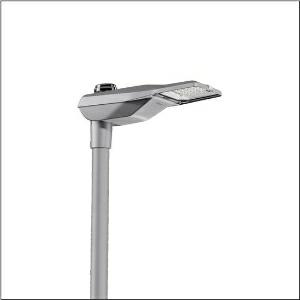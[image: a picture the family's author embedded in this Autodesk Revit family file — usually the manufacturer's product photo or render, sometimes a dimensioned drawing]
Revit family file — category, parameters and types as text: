
# Revit family: streetlight_sl_21_micro___p0_8a_5xe5u27n08db_ddcc
name_source: partatom
category: Lighting Fixtures
units: mm (PartAtom-declared; Revit-internal decimal feet)

## family parameters
Cut with Voids When Loaded = No
Host = Face
Light Source = No
Part Type = Normal
Room Calculation Point = No
Round Connector Dimension = Use Diameter
Shared = No

## types (1)
- --- (1 x LED, 4180 lm, 39.1 W, 2200K)
    Apparent Load = 39 VA
    CIE Flux Codes = 33 69 96 100 100
    Color Rendering = 70
    Color Temperature = 2200K
    Default Elevation = 1800 mm
    Description = Streetlight SL 21 micro, mast luminaire, primary light control with lens, of PMMA, primary optical cover: cover, of toughened safety glass, transparent, light distribution: P0.8a, light emission: direct distribution, primary light characteristic: asymmetric, installation type: post-top, LED, 3G 1.5mm², High Power LED, rated luminous flux: 4.180lm, luminous efficacy: 107lm/W, light colour: 722, colour temperature: 2200K, control gear: NEMA (7pin), control: flexible luminous flux parameterisation, time-dependent luminous flux control, constant luminous flux control, pre-setting: linear dimming characteristic, overheat protection, mains connection: 230..240V, AC, 50/60Hz, connection cable pre-assembled, cable length: 6,5m, wiring characteristics: H07RN-F, start of lifetime: 39W, end of service life: 41W, reduction: 18W, luminaire housing, of diecast aluminium (EN AC-44300), powder-coated, SITECO metallic grey (DB 702S), corrosivity category C5 high according to DIN EN ISO 12944, multi-level sealing system, sealing non-destructively replaceable, inclination adjustable: 0°, 5°, 10°, 15°, length: 528mm, width: 235mm, height: 110mm, spigot size: 76/60mm (post-top), mounting height: 4..8m, protection rating (complete): IP66, insulation class (complete): insulation class I (protective earthing), certification: CE, ENEC, ENEC+, VDE, impact resistance: IK10, permissible operating ambient temperature for outdoor applications: -40..+50°C, standard-compliant lighting for roads and squares, packaging unit: 1 piece

Light Distribution: P0.8a
    Height = 110 mm
    Lamp = 1 x LED
    Lamp Light Flux = 4180 lm
    Lamp Power = 39.1 W
    Lamp count = 1
    Length = 528 mm
    Luminous efficacy = 107 lm/W
    Manufacturer = Siteco
    ModVariant = No
    Model = 5XE5U27N08DB
    Number of Poles = 1
    OnlyDefault = Yes
    Power Factor = 1
    Product Name = Streetlight SL 21 micro | P0.8a
    Product group = mast luminaire | pylon top
    ProductGroupID = 6100
    Protection Class = Protection class I
    Protection Degree = IP 66
    RLX_Detail_Level = 1
    RLX_Emergency_Light_Flux = 0 lm
    RLX_Emergency_Type = 0
    RLX_Emergency_Type_DB = No
    RlxData = <blob elided: 98849 chars, md5=6a1f7258>
    Socket = socket
    Standby Power = 0 W
    System Light Flux = 4180 lm
    System Power = 39 W
    Type Comments = factory setting: luminous flux: 100 % | dim-lin: 254 | 765 mA
    Type Image = l_1294375.jpg
    URL = http://relux.com
    VarID = @adj_081579
    Voltage = 0 V
    Weight = 0.00 kg
    Width = 235 mm

## geometry (parser evidence)
native form markers: Blend x4, Sweep x11
no freeform markers — native parametric forms only
